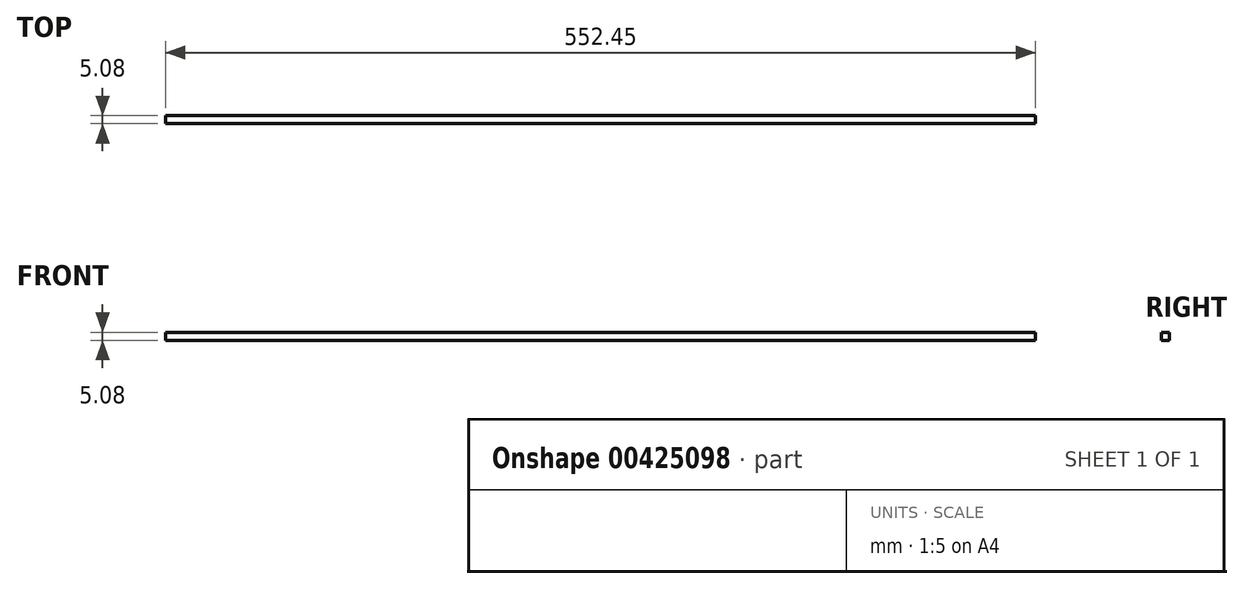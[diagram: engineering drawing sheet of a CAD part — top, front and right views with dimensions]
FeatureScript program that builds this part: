
annotation { "Feature Type Name" : "Feature", "Feature Type Description" : "" }
export const myFeature = defineFeature(function(context is Context, id is Id, definition is map)
    precondition{}
    {
        {
            var Q0;
            Q0=qCreatedBy(makeId("Front.planeOp"),FACE);
            var sketch = newSketch(context, id + "F0", { "sketchPlane" : qUnion([Q0])});
            skLineSegment(sketch, "E0.bottom", {"start": v(-54.62, 41.8) * mm, "end": v(497.83, 41.8) * mm});
            skLineSegment(sketch, "E0.top", {"start": v(-54.62, 36.73) * mm, "end": v(497.83, 36.73) * mm});
            skLineSegment(sketch, "E0.left", {"start": v(-54.62, 41.8) * mm, "end": v(-54.62, 36.73) * mm});
            skLineSegment(sketch, "E0.right", {"start": v(497.83, 41.8) * mm, "end": v(497.83, 36.73) * mm});
            skSolve(sketch);
        }
        {
            var Q0;
            Q0 = qSketchRegion(id + "F0", true);
            extrude(context, id + "F1", {"entities" : qUnion([Q0]), "depth" : 5.08 * mm});
        }
    });
